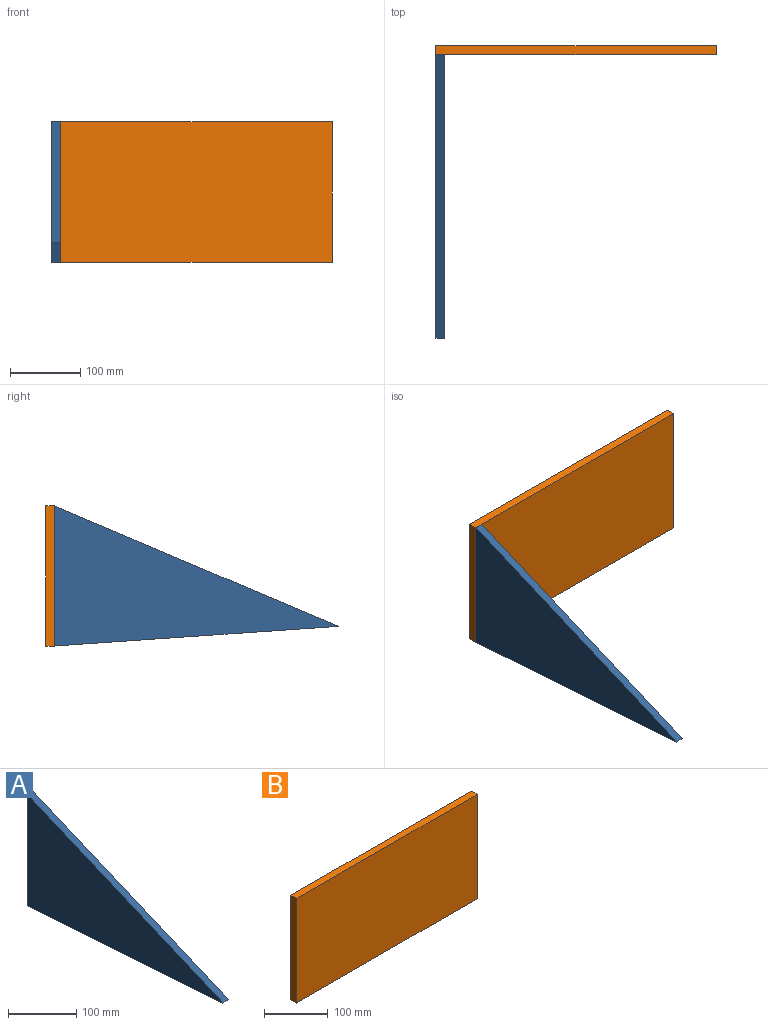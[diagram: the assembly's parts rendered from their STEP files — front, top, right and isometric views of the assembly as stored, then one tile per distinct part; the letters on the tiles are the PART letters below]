
ASSEMBLY  parts=2 mates=1
PART A: 5 faces, bbox 12x405x200 mm
  f0: plane 405.02x28.07mm, normal (0,-0.07,-1), area 4871.9mm2, adj f1,f2,f3,f4
  f1: plane 200x12mm, normal (0,1,0), area 2400mm2, adj f0,f2,f3,f4
  f2: plane 405.02x171.93mm, normal (0,-0.39,0.92), area 5280mm2, adj f0,f1,f3,f4
  f3: plane 405.02x200mm, normal (1,0,0), area 40501.7mm2, adj f0,f1,f2
  f4: plane 405.02x200mm, normal (-1,0,0), area 40501.7mm2, adj f0,f1,f2
PART B: 6 faces, bbox 400x12.7x200 mm
  f0: plane 400x12.7mm, normal (0,0,-1), area 5080mm2, adj f1,f3,f4,f5
  f1: plane 200x12.7mm, normal (1,0,0), area 2540mm2, adj f0,f2,f4,f5
  f2: plane 400x12.7mm, normal (0,0,1), area 5080mm2, adj f1,f3,f4,f5
  f3: plane 200x12.7mm, normal (-1,0,0), area 2540mm2, adj f0,f2,f4,f5
  f4: plane 400x200mm, normal (0,-1,0), area 80000mm2, adj f0,f1,f2,f3
  f5: plane 400x200mm, normal (0,1,0), area 80000mm2, adj f0,f1,f2,f3
PLACE A t=(-412.19,-134.29,-172.94)mm
PLACE B t=(-212.19,126.47,-101.01)mm
MATE fastened A.f4 <-> B.f3  axis (-1,0,0) through (-412.19,113.77,-101.01)mm
